# Revit family: Damper-Manual_Balancing-Carnes-Rectangular-FAEA
name_source: partatom
category: Duct Accessories
revit_build: Autodesk Revit Architecture 2012 (Build: 20110916_2132(x64)
units: mm (PartAtom-declared; Revit-internal decimal feet)

## types (1)
- User Defined Size
    04 CSI = 08 91 00
    95 CSI = 10200
    Assembly Code = D3090700
    Blade Material = Aluminum - Carnes - Extruded
    Catalog URL = http://www.carnes.com
    Connector Description 1 = Duct Connection 1
    Connector Description 2 = Duct Connection 2
    Damper Air Flow = 0 CFM
    Damper Length = 4 1/2"
    Description = Manual Balancing Dampers
    Frame Material = Aluminum - Carnes - Extruded
    Manufacturer = Carnes Company
    Manufacturer Fax = 608-845-6470
    Maximum System Velocity = 2000 FPM
    Model = FAEA
    Pressure Drop = 0.00 Pa
    Product Line = Manual Balancing Dampers
    Product Page URL = http://www.carnes.com
    Specifications  URL = http://www.carnes.com
    Subcategory = Louvers and Dampers
    URL = http://www.carnes.com
    ecoScorecard Product Page = http://ecoscorecard.com

## geometry (parser evidence)
native form markers: Blend x4, Sweep x1
no freeform markers — native parametric forms only
